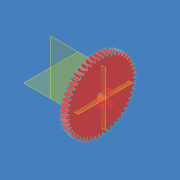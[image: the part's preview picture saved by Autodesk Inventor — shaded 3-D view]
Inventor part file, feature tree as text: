
AUTODESK INVENTOR PART (.ipt)
format: ipt  version: unknown  size: 1,146,368 bytes
history: native  units: mm
features: imported_body x1, hole x1, sketch x1
ambient origin geometry x8: Origin, YZ Plane, XZ Plane, XY Plane, X Axis, Y Axis, Z Axis, Center Point
feature tree (3):
  imported_body  "Basis1"
  hole  "Bohrung2"  [1 undecoded]
  sketch  "Skizze4"  dims[d7=2.8mm d8=6.0mm d9=4.0mm d10=2.0mm d11=90.0deg d12=8.0mm d13=20.594885mm]
note: 1 required parameter value undecoded (feature->parameter linkage not recoverable at this tier; creation-order binding heuristic only, values carry confidence <= 0.55)
